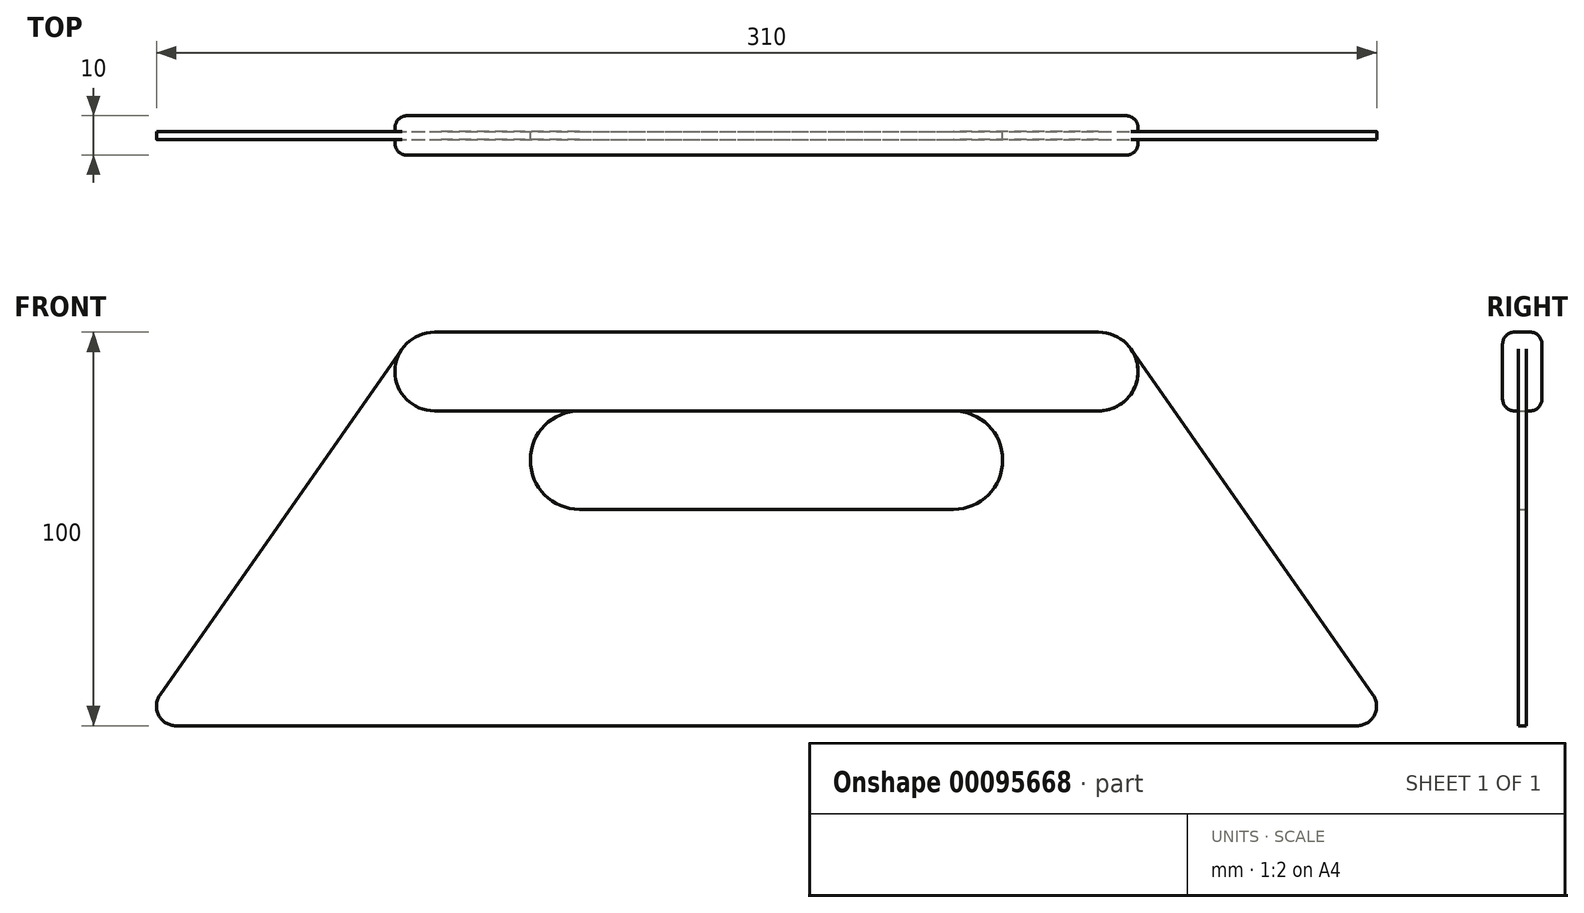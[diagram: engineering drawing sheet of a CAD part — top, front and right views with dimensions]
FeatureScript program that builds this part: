
annotation { "Feature Type Name" : "Feature", "Feature Type Description" : "" }
export const myFeature = defineFeature(function(context is Context, id is Id, definition is map)
    precondition{}
    {
        {
            var Q0;
            Q0=qCreatedBy(makeId("Front.planeOp"),FACE);
            var sketch = newSketch(context, id + "F0", { "sketchPlane" : qUnion([Q0])});
            skLineSegment(sketch, "E0", {"start": v(-150, -50) * mm, "end": v(0, -50) * mm});
            skLineSegment(sketch, "E1", {"start": v(-154.1, -42.13) * mm, "end": v(-89.58, 50) * mm});
            skLineSegment(sketch, "E2", {"start": v(-89.58, 50) * mm, "end": v(0, 50) * mm});
            skPoint(sketch, "E3", {"position": v(-124.6, 0) * mm});
            skLineSegment(sketch, "E4.bottom", {"start": v(-47.5, 30) * mm, "end": v(47.5, 30) * mm});
            skLineSegment(sketch, "E4.top", {"start": v(-47.5, 5) * mm, "end": v(47.5, 5) * mm});
            skLineSegment(sketch, "E4.left", {"start": v(-47.5, 30) * mm, "end": v(-47.5, 5) * mm, "construction": true});
            skLineSegment(sketch, "E4.right", {"start": v(47.5, 30) * mm, "end": v(47.5, 5) * mm, "construction": true});
            skPoint(sketch, "E4.middle", {"position": v(0, 17.5) * mm});
            skArc(sketch, "E5", {"start": v(-47.5, 30) * mm, "mid": v(-60, 17.5) * mm, "end": v(-47.5, 5) * mm});
            skArc(sketch, "E6.MirrorCS", {"start": v(47.5, 30) * mm, "mid": v(60, 17.5) * mm, "end": v(47.5, 5) * mm});
            skPoint(sketch, "E7.visualSharp", {"position": v(-159.6, -50) * mm});
            skArc(sketch, "E7.filletArc", {"start": v(-154.1, -42.13) * mm, "mid": v(-154.44, -47.3) * mm, "end": v(-150, -50) * mm});
            skLineSegment(sketch, "E8.MirrorCS", {"start": v(89.58, 50) * mm, "end": v(0, 50) * mm});
            skLineSegment(sketch, "E9.MirrorCS", {"start": v(154.1, -42.13) * mm, "end": v(89.58, 50) * mm});
            skArc(sketch, "E10.MirrorCS", {"start": v(154.1, -42.13) * mm, "mid": v(154.44, -47.3) * mm, "end": v(150, -50) * mm});
            skLineSegment(sketch, "E11.MirrorCS", {"start": v(150, -50) * mm, "end": v(0, -50) * mm});
            skSolve(sketch);
        }
        {
            var Q0;
            Q0 = qSketchRegion(id + "F0", true);
            extrude(context, id + "F1", {"entities" : qUnion([Q0]), "endBound" : BoundingType.SYMMETRIC, "depth" : 2 * mm});
        }
        {
            var Q0;
            Q0=makeQuery(id+"F1.opExtrude","SWEPT_EDGE",EDGE,{"disambiguationData":[OSD([sQuery(id+"F0.wireOp",EDGE,"E8.MirrorCS"),sQuery(id+"F0.wireOp",EDGE,"E9.MirrorCS")])]});
            var Q1;
            Q1=makeQuery(id+"F1.opExtrude","SWEPT_EDGE",EDGE,{"disambiguationData":[OSD([sQuery(id+"F0.wireOp",EDGE,"E1"),sQuery(id+"F0.wireOp",EDGE,"E2")])]});
            fillet(context, id + "F2", {"entities" : qUnion([Q0, Q1]), "radius" : 10 * mm, "tangentPropagation" : true, "allowEdgeOverflow" : false});
        }
        {
            var Q0;
            Q0=qCreatedBy(makeId("Front.planeOp"),FACE);
            var sketch = newSketch(context, id + "F3", { "sketchPlane" : qUnion([Q0])});
            skLineSegment(sketch, "E12", {"start": v(-84.38, 30) * mm, "end": v(84.38, 30) * mm});
            skPoint(sketch, "E13", {"position": v(0, 30) * mm});
            skLineSegment(sketch, "E14", {"start": v(-84.38, 50) * mm, "end": v(84.38, 50) * mm});
            skArc(sketch, "E15", {"start": v(-84.38, 50) * mm, "mid": v(-94.38, 40) * mm, "end": v(-84.38, 30) * mm});
            skArc(sketch, "E16", {"start": v(84.38, 30) * mm, "mid": v(94.38, 40) * mm, "end": v(84.38, 50) * mm});
            skSolve(sketch);
        }
        {
            var Q0;
            Q0 = qSketchRegion(id + "F3", true);
            extrude(context, id + "F4", {"entities" : qUnion([Q0]), "operationType" : NewBodyOperationType.ADD, "endBound" : BoundingType.SYMMETRIC, "depth" : 10 * mm});
        }
        {
            var Q0;
            Q0=makeQuery(id+"F4.opExtrude","CAP_FACE",FACE,{"disambiguationData":[OSD([sQuery(id+"F3.wireOp",EDGE,"E12"),sQuery(id+"F3.wireOp",EDGE,"E14"),sQuery(id+"F3.wireOp",EDGE,"E15"),sQuery(id+"F3.wireOp",EDGE,"E16")])],"isStart":false});
            var Q1;
            Q1=makeQuery(id+"F4.opExtrude","CAP_FACE",FACE,{"disambiguationData":[OSD([sQuery(id+"F3.wireOp",EDGE,"E12"),sQuery(id+"F3.wireOp",EDGE,"E14"),sQuery(id+"F3.wireOp",EDGE,"E15"),sQuery(id+"F3.wireOp",EDGE,"E16")])],"isStart":true});
            fillet(context, id + "F5", {"entities" : qUnion([Q0, Q1]), "radius" : 3 * mm, "tangentPropagation" : true, "allowEdgeOverflow" : false});
        }
    });
